# Revit family: Deca_Válvula Hydra Duo Pro_2545.C.PRO
name_source: partatom
category: Plumbing Fixtures
revit_build: Autodesk Revit Architecture 2012 (Build: 20120126_0600(x64)
units: mm (PartAtom-declared; Revit-internal decimal feet)

## types (2) — shared parameters
Aprovado por = Contino/quattroD
Assembly Code = D2020300
Atendimento ao Cliente = 0800-0117073
CW Connection = No
Consumo = 3/6 lpf
Criado por = Contino/quattroD
Default Elevation = 1100 mm
Description = Válvula de descarga com duplo acionamento
Diâmetro Saída Agua Fria = 40 mm  [stored 0.131234 ft]
Flow Pressure = 0.00 psi
Informações Complementares = Válvula de duplo acionamento com acabamento anti vandalismo
Linha = Hydra Duo Pro
Louça/Metais = Metal
Manufacturer = Deca
Material = Deca_Corpo: Bronze / Acabamento: Latão Cromado e Plástico de Engenharia
Norma = ABNT NBR 15857: 2011
Peso Liquido (Kg) = 1.19
Pressão = 2 a 40 mca
Produto = Válvula Hydra Duo Pro
Raio Saída Agua Fria = 20 mm  [stored 0.0656168 ft]
Segmento = Hydra
URL = www.deca.com.br/produtos
Variações de COR = Baixa pressão (2545.C.112.PRO); Alta pressão (2545.C.114.PRO)
Válvula = Deca CR10 Cromado Metal
zero-valued in all types: CWFU

## per-type parameters (varying)
| type | Código | Diâmetro Entrada Agua Fria | Model | Raio Entrada Agua Fria |
| 2545.C.112.PRO_Baixa pressão | 2545.C.112.PRO | 40 mm  [stored 0.131234 ft] | 2545.C.112.PRO | 20 mm  [stored 0.0656168 ft] |
| 2545.C.114.PRO_Alta pressão | 2545.C.114.PRO | 32 mm  [stored 0.104987 ft] | 2545.C.114.PRO | 16 mm  [stored 0.0524934 ft] |

note: [stored X ft] marks values corroborated as IEEE doubles in the binary element streams (Revit-internal decimal feet)

## geometry (parser evidence)
native form markers: Blend x4, Sweep x1
no freeform markers — native parametric forms only
